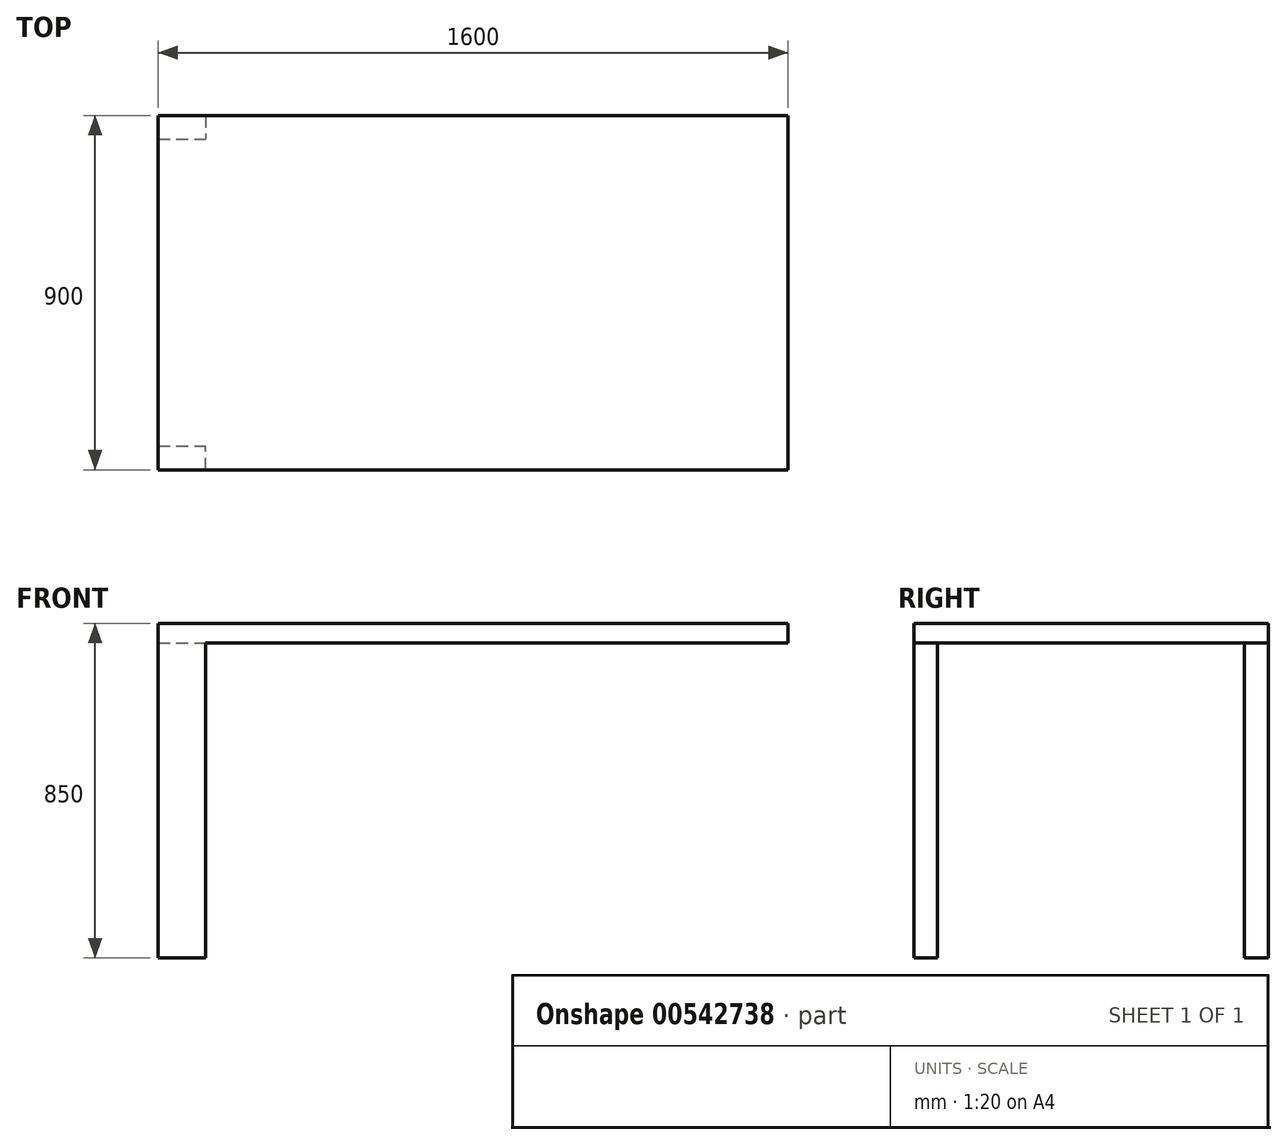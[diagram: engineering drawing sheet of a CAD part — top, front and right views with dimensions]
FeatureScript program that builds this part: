
annotation { "Feature Type Name" : "Feature", "Feature Type Description" : "" }
export const myFeature = defineFeature(function(context is Context, id is Id, definition is map)
    precondition{}
    {
        {
            var Q0;
            Q0=qCreatedBy(makeId("Top.planeOp"),FACE);
            var sketch = newSketch(context, id + "F0", { "sketchPlane" : qUnion([Q0])});
            skLineSegment(sketch, "E0.bottom", {"start": v(-800, 450) * mm, "end": v(800, 450) * mm});
            skLineSegment(sketch, "E0.top", {"start": v(-800, -450) * mm, "end": v(800, -450) * mm});
            skLineSegment(sketch, "E0.left", {"start": v(-800, 450) * mm, "end": v(-800, -450) * mm});
            skLineSegment(sketch, "E0.right", {"start": v(800, 450) * mm, "end": v(800, -450) * mm});
            skPoint(sketch, "E0.middle", {"position": v(0, 0) * mm});
            skSolve(sketch);
        }
        {
            var Q0;
            Q0 = qSketchRegion(id + "F0", true);
            extrude(context, id + "F1", {"entities" : qUnion([Q0]), "depth" : 50 * mm, "offsetDistance" : 25 * mm});
        }
        {
            var Q0;
            Q0=makeQuery(id+"F1.opExtrude","CAP_FACE",FACE,{"disambiguationData":[OSD([sQuery(id+"F0.wireOp",EDGE,"E0.bottom"),sQuery(id+"F0.wireOp",EDGE,"E0.top"),sQuery(id+"F0.wireOp",EDGE,"E0.left"),sQuery(id+"F0.wireOp",EDGE,"E0.right")])],"isStart":true});
            var sketch = newSketch(context, id + "F2", { "sketchPlane" : qUnion([Q0])});
            skLineSegment(sketch, "E1.bottom", {"start": v(-800, 450) * mm, "end": v(-680, 450) * mm});
            skLineSegment(sketch, "E1.top", {"start": v(-800, 390) * mm, "end": v(-680, 390) * mm});
            skLineSegment(sketch, "E1.left", {"start": v(-800, 450) * mm, "end": v(-800, 390) * mm});
            skLineSegment(sketch, "E1.right", {"start": v(-680, 450) * mm, "end": v(-680, 390) * mm});
            skLineSegment(sketch, "E2.bottom", {"start": v(-800, -450) * mm, "end": v(-680, -450) * mm});
            skLineSegment(sketch, "E2.top", {"start": v(-800, -390) * mm, "end": v(-680, -390) * mm});
            skLineSegment(sketch, "E2.left", {"start": v(-800, -450) * mm, "end": v(-800, -390) * mm});
            skLineSegment(sketch, "E2.right", {"start": v(-680, -450) * mm, "end": v(-680, -390) * mm});
            skSolve(sketch);
        }
        {
            var Q0;
            Q0 = qSketchRegion(id + "F2", true);
            extrude(context, id + "F3", {"entities" : qUnion([Q0]), "operationType" : NewBodyOperationType.ADD, "depth" : 800 * mm, "offsetDistance" : 25 * mm});
        }
    });
